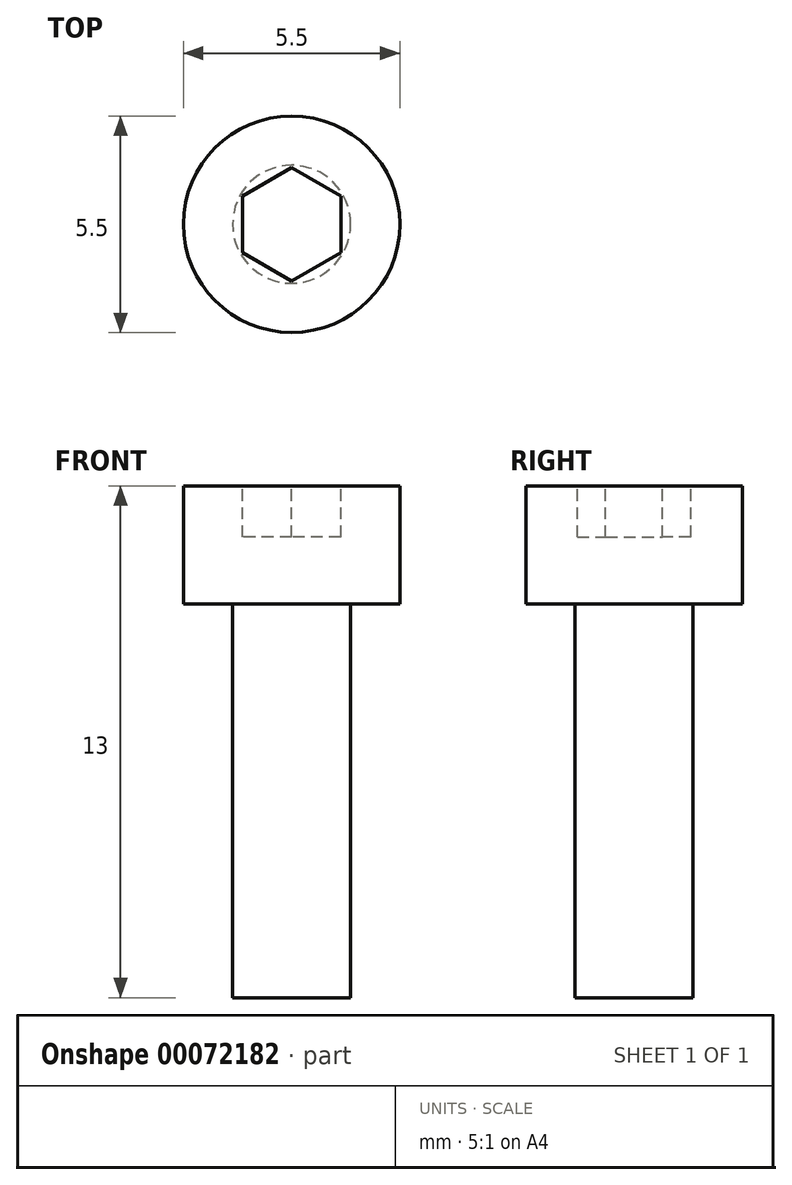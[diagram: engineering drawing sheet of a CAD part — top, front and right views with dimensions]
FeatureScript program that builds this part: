
annotation { "Feature Type Name" : "Feature", "Feature Type Description" : "" }
export const myFeature = defineFeature(function(context is Context, id is Id, definition is map)
    precondition{}
    {
        {
            var Q0;
            Q0=qCreatedBy(makeId("Front.planeOp"),FACE);
            var sketch = newSketch(context, id + "F0", { "sketchPlane" : qUnion([Q0])});
            skLineSegment(sketch, "E0", {"start": v(-1.5, 0) * mm, "end": v(-2.75, 0) * mm});
            skLineSegment(sketch, "E1", {"start": v(-2.75, 0) * mm, "end": v(-2.75, 3) * mm});
            skLineSegment(sketch, "E2", {"start": v(-2.75, 3) * mm, "end": v(0, 3) * mm});
            skLineSegment(sketch, "E3", {"start": v(0, 3) * mm, "end": v(0, 0) * mm});
            skLineSegment(sketch, "E4", {"start": v(-1.5, 0) * mm, "end": v(-1.5, -10) * mm});
            skLineSegment(sketch, "E5", {"start": v(-1.5, -10) * mm, "end": v(0, -10) * mm});
            skLineSegment(sketch, "E6", {"start": v(0, -10) * mm, "end": v(0, 0) * mm});
            skLineSegment(sketch, "E7", {"start": v(0, 3) * mm, "end": v(0, 8.62) * mm, "construction": true});
            skSolve(sketch);
        }
        {
            var Q0;
            Q0=makeQuery(id+"F0.imprint","IMPRINT",FACE,{"disambiguationData":[TD([[makeQuery(id+"F0.imprint","IMPRINT",EDGE,{"derivedFrom":sQuery(id+"F0.wireOp",EDGE,"E0")}),-1.0]])]});
            var Q1;
            Q1=sQuery(id+"F0.wireOp",EDGE,"E6");
            revolve(context, id + "F1", {"entities" : qUnion([Q0]), "axis" : qUnion([Q1]), "revolveType" : RevolveType.FULL});
        }
        {
            var Q0;
            Q0=makeQuery(id+"F1.opRevolve","SWEPT_FACE",FACE,{"disambiguationData":[OSD([sQuery(id+"F0.wireOp",EDGE,"E2")])]});
            var sketch = newSketch(context, id + "F2", { "sketchPlane" : qUnion([Q0])});
            skCircle(sketch, "E8.cCircle", {"center": v(0, 0) * mm, "radius": 1.25 * mm, "construction": true});
            skLineSegment(sketch, "E8.0", {"start": v(-1.25, -0.72) * mm, "end": v(-1.25, 0.72) * mm});
            skLineSegment(sketch, "E8.1", {"start": v(-1.25, 0.72) * mm, "end": v(0, 1.44) * mm});
            skLineSegment(sketch, "E8.2", {"start": v(0, 1.44) * mm, "end": v(1.25, 0.72) * mm});
            skLineSegment(sketch, "E8.3", {"start": v(1.25, 0.72) * mm, "end": v(1.25, -0.72) * mm});
            skLineSegment(sketch, "E8.4", {"start": v(1.25, -0.72) * mm, "end": v(0, -1.44) * mm});
            skLineSegment(sketch, "E8.5", {"start": v(0, -1.44) * mm, "end": v(-1.25, -0.72) * mm});
            skPoint(sketch, "E8.0.midPoint", {"position": v(-1.25, 0) * mm});
            skSolve(sketch);
        }
        {
            var Q0;
            Q0 = qSketchRegion(id + "F2", true);
            extrude(context, id + "F3", {"entities" : qUnion([Q0]), "operationType" : NewBodyOperationType.REMOVE, "oppositeDirection" : true, "depth" : 1.3 * mm});
        }
    });
